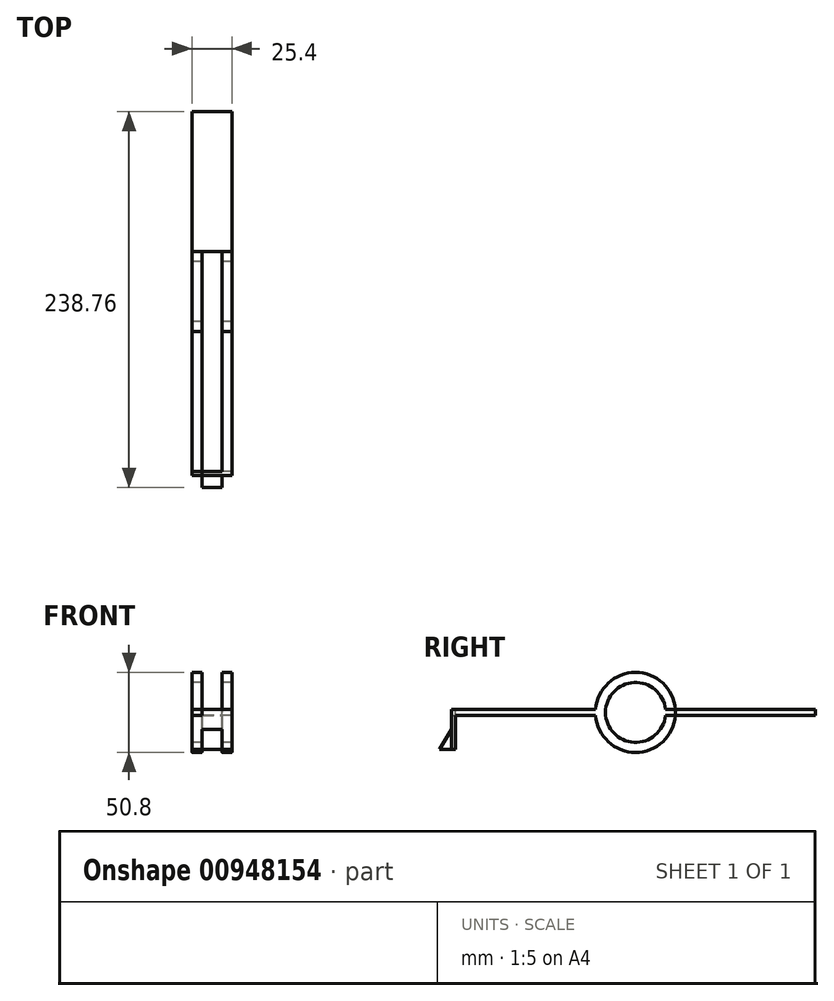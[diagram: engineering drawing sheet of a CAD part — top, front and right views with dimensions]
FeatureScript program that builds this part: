
annotation { "Feature Type Name" : "Feature", "Feature Type Description" : "" }
export const myFeature = defineFeature(function(context is Context, id is Id, definition is map)
    precondition{}
    {
        {
            var Q0;
            Q0=qCreatedBy(makeId("Right.planeOp"),FACE);
            var sketch = newSketch(context, id + "F0", { "sketchPlane" : qUnion([Q0])});
            skCircle(sketch, "E0", {"center": v(-55.2, 18.3) * mm, "radius": 25.4 * mm});
            skLineSegment(sketch, "E1.bottom", {"start": v(-29.8, 18.3) * mm, "end": v(59.1, 18.3) * mm});
            skLineSegment(sketch, "E1.top", {"start": v(-29.8, 16.4) * mm, "end": v(59.1, 16.4) * mm});
            skLineSegment(sketch, "E1.left", {"start": v(-29.8, 18.3) * mm, "end": v(-29.8, 16.4) * mm});
            skLineSegment(sketch, "E1.right", {"start": v(59.1, 18.3) * mm, "end": v(59.1, 16.4) * mm});
            skLineSegment(sketch, "E2.top", {"start": v(-29.8, 20.21) * mm, "end": v(59.1, 20.21) * mm});
            skLineSegment(sketch, "E2.left", {"start": v(-29.8, 18.3) * mm, "end": v(-29.8, 20.21) * mm});
            skLineSegment(sketch, "E2.right", {"start": v(59.1, 18.3) * mm, "end": v(59.1, 20.21) * mm});
            skCircle(sketch, "E3", {"center": v(-55.2, 18.3) * mm, "radius": 19.05 * mm});
            skLineSegment(sketch, "E4.bottom", {"start": v(-29.8, 20.21) * mm, "end": v(-169.5, 20.21) * mm});
            skLineSegment(sketch, "E4.top", {"start": v(-29.8, 16.4) * mm, "end": v(-169.5, 16.4) * mm});
            skLineSegment(sketch, "E4.left", {"start": v(-29.8, 20.21) * mm, "end": v(-29.8, 16.4) * mm});
            skLineSegment(sketch, "E4.right", {"start": v(-169.5, 20.21) * mm, "end": v(-169.5, 16.4) * mm});
            skSolve(sketch);
        }
        {
            var Q0;
            {var subQ0=sQuery(id+"F0.wireOp",EDGE,"E1.bottom");Q0=makeQuery(id+"F0.imprint","IMPRINT",FACE,{"disambiguationData":[TD([[makeQuery(id+"F0.imprint","IMPRINT",EDGE,{"derivedFrom":subQ0}),1.0]])]});}
            var Q1;
            {var subQ0=sQuery(id+"F0.wireOp",EDGE,"E1.top");Q1=makeQuery(id+"F0.imprint","IMPRINT",FACE,{"disambiguationData":[TD([[makeQuery(id+"F0.imprint","IMPRINT",EDGE,{"derivedFrom":subQ0}),1.0]])]});}
            var Q2;
            {var subQ1=sQuery(id+"F0.wireOp",EDGE,"E0");var subQ3=sQuery(id+"F0.wireOp",EDGE,"E4.bottom");var subQ4=makeQuery(id+"F0.imprint","INTERSECT",VERTEX,{"disambiguationData":[OD(0.0)],"derivedFrom":[subQ1,subQ3]});Q2=makeQuery(id+"F0.imprint","IMPRINT",FACE,{"disambiguationData":[TD([[makeQuery(id+"F0.imprint","IMPRINT",EDGE,{"disambiguationData":[TD([[subQ4,1.0]])],"derivedFrom":subQ1}),-1.0]])]});}
            var Q3;
            {var subQ1=sQuery(id+"F0.wireOp",EDGE,"E0");var subQ3=sQuery(id+"F0.wireOp",EDGE,"E4.top");var subQ4=makeQuery(id+"F0.imprint","INTERSECT",VERTEX,{"disambiguationData":[OD(1.0)],"derivedFrom":[subQ1,subQ3]});Q3=makeQuery(id+"F0.imprint","IMPRINT",FACE,{"disambiguationData":[TD([[makeQuery(id+"F0.imprint","IMPRINT",EDGE,{"disambiguationData":[TD([[subQ4,-1.0]])],"derivedFrom":subQ1}),-1.0]])]});}
            var Q4;
            {var subQ0=sQuery(id+"F0.wireOp",EDGE,"E4.bottom");var subQ1=sQuery(id+"F0.wireOp",EDGE,"E3");var subQ2=makeQuery(id+"F0.imprint","INTERSECT",VERTEX,{"disambiguationData":[OD(1.0)],"derivedFrom":[subQ1,subQ0]});Q4=makeQuery(id+"F0.imprint","IMPRINT",FACE,{"disambiguationData":[TD([[makeQuery(id+"F0.imprint","IMPRINT",EDGE,{"disambiguationData":[TD([[subQ2,1.0]])],"derivedFrom":subQ1}),-1.0]])]});}
            var Q5;
            {var subQ0=sQuery(id+"F0.wireOp",EDGE,"E4.bottom");var subQ1=sQuery(id+"F0.wireOp",EDGE,"E0");var subQ2=makeQuery(id+"F0.imprint","INTERSECT",VERTEX,{"disambiguationData":[OD(0.0)],"derivedFrom":[subQ1,subQ0]});Q5=makeQuery(id+"F0.imprint","IMPRINT",FACE,{"disambiguationData":[TD([[makeQuery(id+"F0.imprint","IMPRINT",EDGE,{"disambiguationData":[TD([[subQ2,-1.0]])],"derivedFrom":subQ1}),1.0]])]});}
            var Q6;
            {var subQ0=sQuery(id+"F0.wireOp",EDGE,"E4.top");var subQ1=sQuery(id+"F0.wireOp",EDGE,"E0");var subQ2=makeQuery(id+"F0.imprint","INTERSECT",VERTEX,{"disambiguationData":[OD(0.0)],"derivedFrom":[subQ1,subQ0]});Q6=makeQuery(id+"F0.imprint","IMPRINT",FACE,{"disambiguationData":[TD([[makeQuery(id+"F0.imprint","IMPRINT",EDGE,{"disambiguationData":[TD([[subQ2,-1.0]])],"derivedFrom":subQ1}),1.0]])]});}
            var Q7;
            {var subQ0=sQuery(id+"F0.wireOp",EDGE,"E4.bottom");var subQ1=sQuery(id+"F0.wireOp",EDGE,"E0");var subQ2=makeQuery(id+"F0.imprint","INTERSECT",VERTEX,{"disambiguationData":[OD(1.0)],"derivedFrom":[subQ1,subQ0]});Q7=makeQuery(id+"F0.imprint","IMPRINT",FACE,{"disambiguationData":[TD([[makeQuery(id+"F0.imprint","IMPRINT",EDGE,{"disambiguationData":[TD([[subQ2,-1.0]])],"derivedFrom":subQ1}),1.0]])]});}
            var Q8;
            {var subQ5=sQuery(id+"F0.wireOp",EDGE,"E4.right");Q8=makeQuery(id+"F0.imprint","IMPRINT",FACE,{"disambiguationData":[TD([[makeQuery(id+"F0.imprint","IMPRINT",EDGE,{"derivedFrom":subQ5}),1.0]])]});}
            extrude(context, id + "F1", {"entities" : qUnion([Q0, Q1, Q2, Q3, Q4, Q5, Q6, Q7, Q8]), "depth" : 25.4 * mm, "offsetDistance" : 25.4 * mm});
        }
        {
            var Q0;
            Q0=makeQuery(id+"F1.opExtrude","SWEPT_FACE",FACE,{"disambiguationData":[OSD([sQuery(id+"F0.wireOp",EDGE,"E4.bottom")])]});
            var sketch = newSketch(context, id + "F2", { "sketchPlane" : qUnion([Q0])});
            skLineSegment(sketch, "E5.bottom", {"start": v(6.35, -169.5) * mm, "end": v(19.05, -169.5) * mm});
            skLineSegment(sketch, "E5.top", {"start": v(6.35, -29.8) * mm, "end": v(19.05, -29.8) * mm});
            skLineSegment(sketch, "E5.left", {"start": v(6.35, -169.5) * mm, "end": v(6.35, -29.8) * mm});
            skLineSegment(sketch, "E5.right", {"start": v(19.05, -169.5) * mm, "end": v(19.05, -29.8) * mm});
            skSolve(sketch);
        }
        {
            var Q0;
            {var subQ0=sQuery(id+"F2.wireOp",EDGE,"E5.bottom");Q0=makeQuery(id+"F2.imprint","IMPRINT",FACE,{"disambiguationData":[TD([[makeQuery(id+"F2.imprint","IMPRINT",EDGE,{"derivedFrom":subQ0}),-1.0]])]});}
            var Q1;
            {var subQ0=sQuery(id+"F2.wireOp",EDGE,"E5.top");Q1=makeQuery(id+"F2.imprint","IMPRINT",FACE,{"disambiguationData":[TD([[makeQuery(id+"F2.imprint","IMPRINT",EDGE,{"derivedFrom":subQ0}),-1.0]])]});}
            extrude(context, id + "F3", {"entities" : qUnion([Q0, Q1]), "operationType" : NewBodyOperationType.REMOVE, "oppositeDirection" : true, "depth" : 50.8 * mm, "offsetDistance" : 25.4 * mm, "hasSecondDirection" : true, "secondDirectionOppositeDirection" : false, "secondDirectionDepth" : 25.4 * mm});
        }
        {
            var Q0;
            {var subQ0=sQuery(id+"F0.wireOp",EDGE,"E4.right");Q0=makeQuery(id+"F3.boolean.opBoolean","SPLIT",FACE,{"disambiguationData":[TD([makeQuery(id+"F3.opExtrude","SWEPT_FACE",FACE,{"disambiguationData":[OSD([sQuery(id+"F2.wireOp",EDGE,"E5.left")])]})])],"derivedFrom":makeQuery(id+"F1.opExtrude","SWEPT_FACE",FACE,{"disambiguationData":[OSD([subQ0])]})});}
            var sketch = newSketch(context, id + "F4", { "sketchPlane" : qUnion([Q0])});
            skLineSegment(sketch, "E6.bottom", {"start": v(0, 20.21) * mm, "end": v(25.4, 20.21) * mm});
            skLineSegment(sketch, "E6.top", {"start": v(0, -5.19) * mm, "end": v(25.4, -5.19) * mm});
            skLineSegment(sketch, "E6.left", {"start": v(0, 20.21) * mm, "end": v(0, -5.19) * mm});
            skLineSegment(sketch, "E6.right", {"start": v(25.4, 20.21) * mm, "end": v(25.4, -5.19) * mm});
            skSolve(sketch);
        }
        {
            var Q0;
            {var subQ6=sQuery(id+"F4.wireOp",EDGE,"E6.top");Q0=makeQuery(id+"F4.imprint","IMPRINT",FACE,{"disambiguationData":[TD([[makeQuery(id+"F4.imprint","IMPRINT",EDGE,{"derivedFrom":subQ6}),1.0]])]});}
            var Q1;
            {var subQ3=sQuery(id+"F2.wireOp",EDGE,"E5.left");var subQ4=sQuery(id+"F0.wireOp",EDGE,"E4.right");var subQ5=sQuery(id+"F0.wireOp",EDGE,"E4.bottom");var subQ6=makeQuery(id+"F3.boolean.opBoolean","COPY",EDGE,{"derivedFrom":makeQuery(id+"F3.opExtrude","SWEPT_EDGE",EDGE,{"disambiguationData":[OSD([subQ5,subQ4,sQuery(id+"F2.wireOp",EDGE,"E5.bottom"),subQ3])]})});Q1=makeQuery(id+"F4.imprint","IMPRINT",FACE,{"disambiguationData":[TD([[makeQuery(id+"F4.imprint","IMPRINT",EDGE,{"derivedFrom":subQ6}),1.0]])]});}
            extrude(context, id + "F5", {"entities" : qUnion([Q0, Q1]), "operationType" : NewBodyOperationType.ADD, "depth" : 2.54 * mm, "offsetDistance" : 25.4 * mm});
        }
        {
            var Q0;
            Q0=makeQuery(id+"F5.opExtrude","CAP_FACE",FACE,{"disambiguationData":[OSD([sQuery(id+"F4.wireOp",EDGE,"E6.bottom"),sQuery(id+"F4.wireOp",EDGE,"E6.top"),sQuery(id+"F4.wireOp",EDGE,"E6.left"),sQuery(id+"F4.wireOp",EDGE,"E6.right")])],"isStart":false});
            var sketch = newSketch(context, id + "F6", { "sketchPlane" : qUnion([Q0])});
            skLineSegment(sketch, "E7.bottom", {"start": v(6.35, -5.19) * mm, "end": v(19.05, -5.19) * mm});
            skLineSegment(sketch, "E7.top", {"start": v(6.35, 7.51) * mm, "end": v(19.05, 7.51) * mm});
            skLineSegment(sketch, "E7.left", {"start": v(6.35, -5.19) * mm, "end": v(6.35, 7.51) * mm});
            skLineSegment(sketch, "E7.right", {"start": v(19.05, -5.19) * mm, "end": v(19.05, 7.51) * mm});
            skSolve(sketch);
        }
        {
            var Q0;
            Q0=makeQuery(id+"F6.imprint","IMPRINT",FACE,{"disambiguationData":[TD([[makeQuery(id+"F6.imprint","IMPRINT",EDGE,{"derivedFrom":sQuery(id+"F6.wireOp",EDGE,"E7.bottom")}),1.0]])]});
            extrude(context, id + "F7", {"entities" : qUnion([Q0]), "operationType" : NewBodyOperationType.ADD, "depth" : 7.62 * mm, "offsetDistance" : 25.4 * mm});
        }
        {
            var Q0;
            Q0=makeQuery(id+"F7.opExtrude","SWEPT_FACE",FACE,{"disambiguationData":[OSD([sQuery(id+"F6.wireOp",EDGE,"E7.right")])]});
            var sketch = newSketch(context, id + "F8", { "sketchPlane" : qUnion([Q0])});
            skLineSegment(sketch, "E8", {"start": v(-179.67, -5.19) * mm, "end": v(-172.05, 7.51) * mm});
            skSolve(sketch);
        }
        {
            var Q0;
            Q0=makeQuery(id+"F8.imprint","IMPRINT",FACE,{"disambiguationData":[TD([[makeQuery(id+"F8.imprint","IMPRINT",EDGE,{"derivedFrom":sQuery(id+"F8.wireOp",EDGE,"E8")}),1.0]])]});
            extrude(context, id + "F9", {"entities" : qUnion([Q0]), "operationType" : NewBodyOperationType.REMOVE, "oppositeDirection" : true, "depth" : 25.4 * mm, "offsetDistance" : 25.4 * mm});
        }
    });
